# Revit family: Agta_Record_SldngDrset_THERMCORD-E-STA_WallBased
name_source: partatom
category: Doors
revit_build: Autodesk Revit Architecture 2012 (Build: 20110916_2132(x64)
units: mm (PartAtom-declared; Revit-internal decimal feet)

## types (8) — shared parameters
AccessoryOptions = Contact manufacturer
AlternativeDoorsetGlazing = Part of glazing spec
AntiFingerTrapRequirement = Yes
Assembly Code = B2030110
BIMObjectName = THERMCORD E-STA - Wall based.rfa
ClearHeightOfPassage = 2150.00 mm
Clearance Zones = No
Colour = Customer specific
Configuration = 1 or 2
Construction Type = Automatic Sliding Door
Description = Automatic Sliding Door
DoorIncluded = Yes
DoorOpening = 0.00 mm
DoorOpeningLeft = 1246.00 mm
DoorOpeningRight = 1246.00 mm
DoorsetFasteners = Screws
DoorsetOperation = Automatic
Drive Depth = 210.00 mm
DriveUnit = Sliding Door, Sheet Metal (Painted Steel)
ElectronicLock = Yes
ExtraLeft = 0.00 mm
ExtraRight = 0.00 mm
ExtraWidthLeft = 0.00 mm
ExtraWidthRight = 0.00 mm
Finish = Powder coated, Anodized, customer specific
FireExit = No
FloorGuide = Sliding Door, Stainless Steel
FrameMaterial = Aluminium
FrameProfile = Aluminium
FrameSeal = Yes
GlassLayers = 2
GlassThickness1 = 8 mm (default)
GlassThickness2 = None (default)
GlassType = Part of glazing spec
HandicapAccessible = Yes
HasDrive = Yes
Inner Panel Width = 1246.00 mm
IsExternal = Yes
LeafColourOptions = All RAL, customer specific
Left Profile = No
Manufacturer = Record
ManufacturerName = Record
ManufacturerURL = www.agta-record.com
Material = Aluminium
Model = THERMCORD E-STA
ModelReference = Depends on the configuration
NBSDescription = Automatic Sliding Door
NBSReference = 25-50-20/175
NominalLength = 0.00 mm
OffsetFromInteriorWallFace(OnlyApplicableForTypesWithTwoSidePanels) = 0.00 mm
OffsetFromWallSide = 0.00 mm
OffsetFromWallTop = 0.00 mm
Opening = 0.00 mm
Opening Width in Wall = 1060.00 mm
OpeningWidth = 1200.00 mm
Panel Height = 2200.00 mm
PanelFill = Sliding Door, Laminated Safety Glass (Clear)
PanelFrames = Sliding Door, Aluminium
ProductInformation = www.agta-record.com
ReferenceStandard = EN16005, EN16361, DIN 18650, etc.
ReplacementCost = Depends on the configuration and door type
Right Profile = No
Rough Width = 2503.00 mm
SelfClosing = Yes
ServiceLifeDuration = 10-15 years
Shape = Rectangular
Side Panel Minimum Standard = 1246.00 mm
Side Panel Width Left = 1246.00 mm
Side Panel Width Right = 1246.00 mm
SmokeStop = No
SupportLength = 2497.00 mm
Thickness = 0.00 mm
ThresholdRequired = Yes
ThresholdStripping = No additional required, part of the doorset
URL = www.agta-record.com
Uniclass2 = Ss_25_30_20_77
Version = Version 1.0
WarrantyDescription = Depends on country
WarrantyDurationLabour = Depends on country
WarrantyDurationParts = Depends on country
WarrantyDurationUnit = Depends on country
WarrantyGuarantorLabour = Local door manufacturer
WarrantyGuarantorParts = Local door manufacturer
WarrantyStartDate = Depends on country
Weight = Depends on configuration and size
WithDriveCladding = Yes
WithinStandardSizes = Yes
WithoutDriveCladding(OnlyApplicableForTypesWithoutSidePanels) = No
zero-valued in all types: Cost, ThermalTransmittance

## per-type parameters (varying)
| type | DoorSeal | DriveUnitHeight | Height | IfcExportAs | IfcExportType | Interlacing profile 1 | Interlacing profile left | Interlacing profile right | Left Panel | NominalHeight | NominalWidth | Right Panel | Rough Height | Side void left | Side void right | SupportLengthLeft | SupportLengthRight | TotalHeight | TotalWidth | WallMountingProfile | Width |
| THERMCORD E-STA-L 150mm drive unit height - left - with side panel | yes | 150.00 mm | 2300.00 mm |  |  | Yes | Yes | No | Yes | 2300.00 mm | 2497.00 mm | No | 2306.00 mm | 1175.50 mm | 46.00 mm | 1823.00 mm | 674.00 mm | 2300.00 mm | 2497.00 mm | Yes | 2497.00 mm |
| THERMCORD E-STA-L 150mm drive unit height - left - without side panels | 1 | 150.00 mm | 2300.00 mm |  |  | No | Yes | No | No | 2300.00 mm | 1305.50 mm | No | 2306.00 mm | 0.00 mm | 46.00 mm | 1823.00 mm | 674.00 mm | 2300.00 mm | 1305.50 mm | No | 1305.50 mm |
| THERMCORD E-STA-R 150mm drive unit height - right - with side panel | 1 | 150.00 mm | 2300.00 mm |  |  | Yes | No | Yes | No | 2300.00 mm | 2497.00 mm | Yes | 2306.00 mm | 46.00 mm | 1175.50 mm | 674.00 mm | 1823.00 mm | 2300.00 mm | 2497.00 mm | Yes | 2497.00 mm |
| THERMCORD E-STA-R 150mm drive unit height - right - without side panels | 1 | 150.00 mm | 2300.00 mm |  |  | No | No | Yes | No | 2300.00 mm | 1305.50 mm | No | 2306.00 mm | 46.00 mm | 0.00 mm | 674.00 mm | 1823.00 mm | 2300.00 mm | 1305.50 mm | No | 1305.50 mm |
| THERMCORD E-STA-L 200mm drive unit height - left - with side panel | 1 | 200.00 mm | 2350.00 mm | IfcDoorStyle | Door | Yes | Yes | No | Yes | 2350.00 mm | 2497.00 mm | No | 2356.00 mm | 1175.50 mm | 46.00 mm | 1823.00 mm | 674.00 mm | 2350.00 mm | 2497.00 mm | Yes | 2497.00 mm |
| THERMCORD E-STA-L 200mm drive unit height - left - without side panels | 1 | 200.00 mm | 2350.00 mm |  |  | No | Yes | No | No | 2350.00 mm | 1305.50 mm | No | 2356.00 mm | 0.00 mm | 46.00 mm | 1823.00 mm | 674.00 mm | 2350.00 mm | 1305.50 mm | No | 1305.50 mm |
| THERMCORD E-STA-R 200mm drive unit height - right - with side panel | 1 | 200.00 mm | 2350.00 mm |  |  | Yes | No | Yes | No | 2350.00 mm | 2497.00 mm | Yes | 2356.00 mm | 46.00 mm | 1175.50 mm | 674.00 mm | 1823.00 mm | 2350.00 mm | 2497.00 mm | Yes | 2497.00 mm |
| THERMCORD E-STA-R 200mm drive unit height - right - without side panels | 1 | 200.00 mm | 2350.00 mm |  |  | No | No | Yes | No | 2350.00 mm | 1305.50 mm | No | 2356.00 mm | 46.00 mm | 0.00 mm | 674.00 mm | 1823.00 mm | 2350.00 mm | 1305.50 mm | No | 1305.50 mm |

## geometry (parser evidence)
native form markers: Sweep x18
no freeform markers — native parametric forms only
